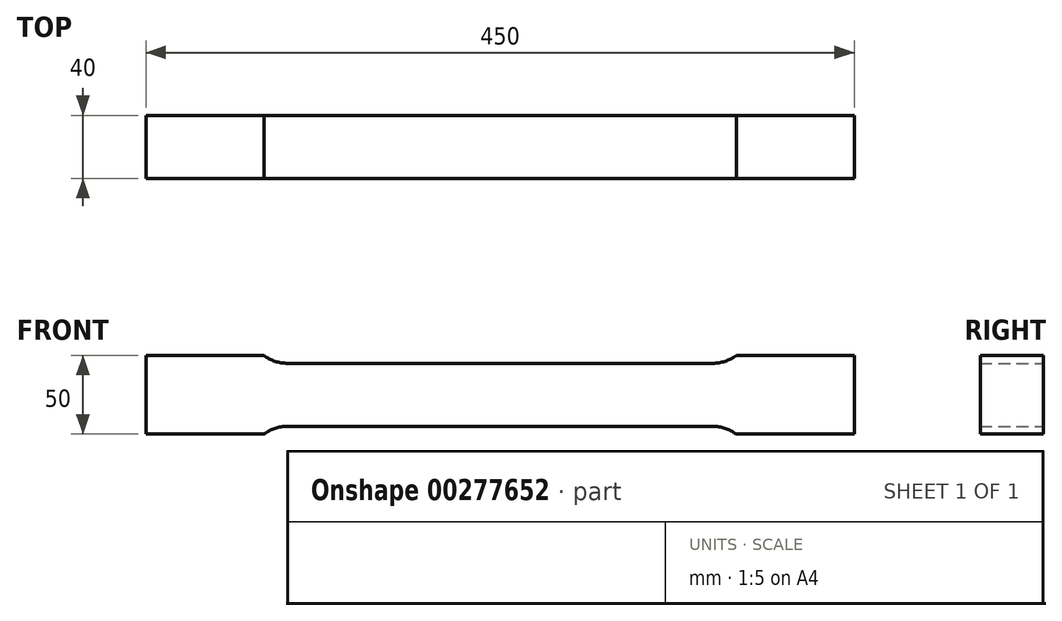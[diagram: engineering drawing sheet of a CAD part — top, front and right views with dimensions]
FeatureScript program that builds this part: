
annotation { "Feature Type Name" : "Feature", "Feature Type Description" : "" }
export const myFeature = defineFeature(function(context is Context, id is Id, definition is map)
    precondition{}
    {
        {
            var Q0;
            Q0=qCreatedBy(makeId("Front.planeOp"),FACE);
            var sketch = newSketch(context, id + "F0", { "sketchPlane" : qUnion([Q0])});
            skLineSegment(sketch, "E0", {"start": v(0, 20) * mm, "end": v(135, 20) * mm});
            skArc(sketch, "E1", {"start": v(135, 20) * mm, "mid": v(142.9, 21.28) * mm, "end": v(150, 25) * mm});
            skLineSegment(sketch, "E2", {"start": v(150, 25) * mm, "end": v(225, 25) * mm});
            skLineSegment(sketch, "E3", {"start": v(225, 25) * mm, "end": v(225, 0) * mm});
            skArc(sketch, "E4.MirrorCS", {"start": v(135, -20) * mm, "mid": v(142.9, -21.28) * mm, "end": v(150, -25) * mm});
            skLineSegment(sketch, "E5.MirrorCS", {"start": v(150, -25) * mm, "end": v(225, -25) * mm});
            skLineSegment(sketch, "E6.MirrorCS", {"start": v(0, -20) * mm, "end": v(135, -20) * mm});
            skLineSegment(sketch, "E7.MirrorCS", {"start": v(225, -25) * mm, "end": v(225, 0) * mm});
            skLineSegment(sketch, "E8.MirrorCS", {"start": v(-225, -25) * mm, "end": v(-225, 0) * mm});
            skLineSegment(sketch, "E9.MirrorCS", {"start": v(0, 20) * mm, "end": v(-135, 20) * mm});
            skLineSegment(sketch, "E10.MirrorCS", {"start": v(0, -20) * mm, "end": v(-135, -20) * mm});
            skArc(sketch, "E11.MirrorCS", {"start": v(-135, -20) * mm, "mid": v(-142.9, -21.28) * mm, "end": v(-150, -25) * mm});
            skArc(sketch, "E12.MirrorCS", {"start": v(-135, 20) * mm, "mid": v(-142.9, 21.28) * mm, "end": v(-150, 25) * mm});
            skLineSegment(sketch, "E13.MirrorCS", {"start": v(-150, -25) * mm, "end": v(-225, -25) * mm});
            skLineSegment(sketch, "E14.MirrorCS", {"start": v(-150, 25) * mm, "end": v(-225, 25) * mm});
            skLineSegment(sketch, "E15.MirrorCS", {"start": v(-225, 25) * mm, "end": v(-225, 0) * mm});
            skSolve(sketch);
        }
        {
            var Q0;
            Q0 = qSketchRegion(id + "F0", true);
            extrude(context, id + "F1", {"entities" : qUnion([Q0]), "endBound" : BoundingType.SYMMETRIC, "depth" : 40 * mm});
        }
    });
